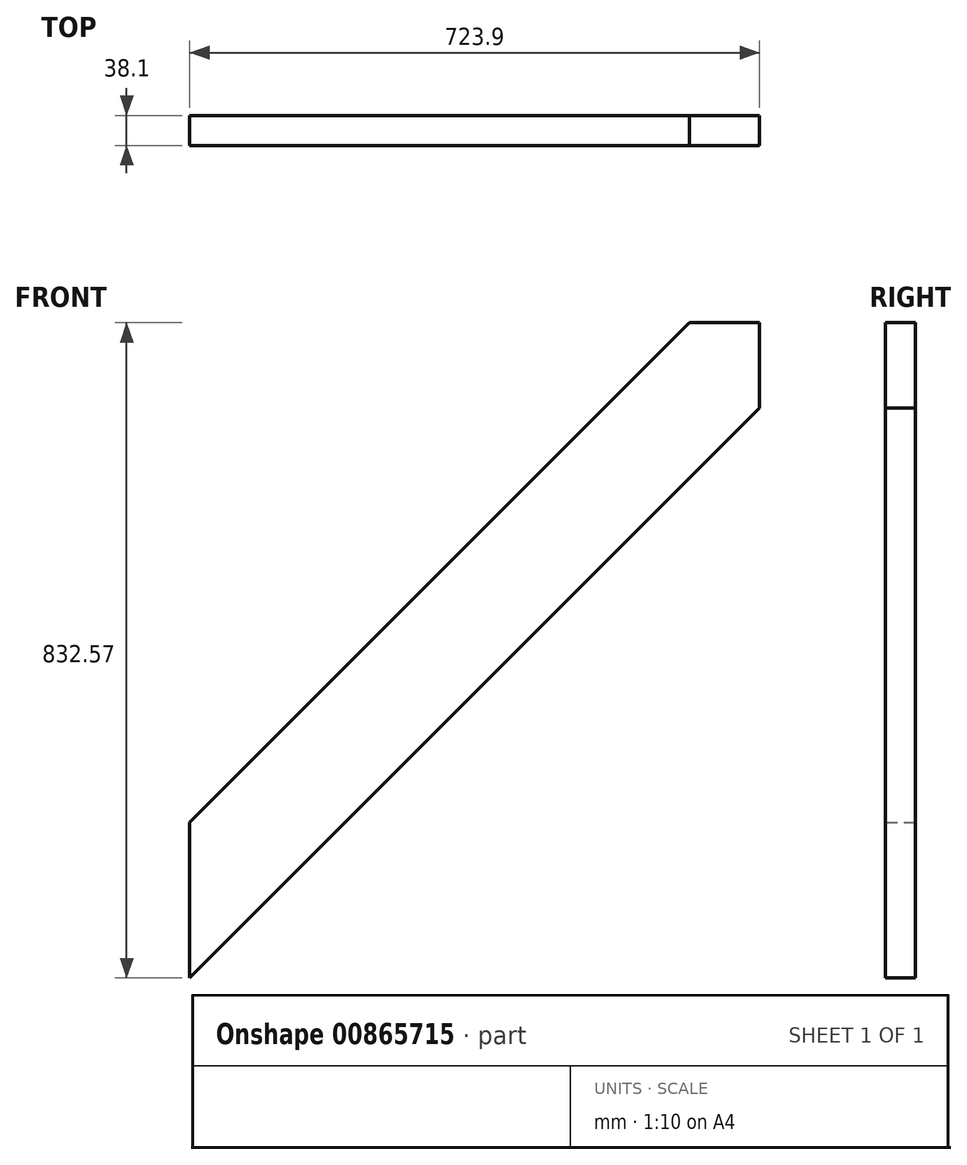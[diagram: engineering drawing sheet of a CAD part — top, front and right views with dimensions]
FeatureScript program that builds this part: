
annotation { "Feature Type Name" : "Feature", "Feature Type Description" : "" }
export const myFeature = defineFeature(function(context is Context, id is Id, definition is map)
    precondition{}
    {
        {
            var Q0;
            Q0=qCreatedBy(makeId("Front.planeOp"),FACE);
            var sketch = newSketch(context, id + "F0", { "sketchPlane" : qUnion([Q0])});
            skLineSegment(sketch, "E0", {"start": v(0, 0) * mm, "end": v(0, 197.57) * mm});
            skLineSegment(sketch, "E1", {"start": v(0, 197.57) * mm, "end": v(635, 832.57) * mm});
            skLineSegment(sketch, "E2", {"start": v(635, 832.57) * mm, "end": v(723.9, 832.57) * mm});
            skLineSegment(sketch, "E3", {"start": v(723.9, 832.57) * mm, "end": v(723.9, 723.9) * mm});
            skLineSegment(sketch, "E4", {"start": v(723.9, 723.9) * mm, "end": v(0, 0) * mm});
            skSolve(sketch);
        }
        {
            var Q0;
            Q0=makeQuery(id+"F0.imprint","IMPRINT",FACE,{"disambiguationData":[TD([[makeQuery(id+"F0.imprint","IMPRINT",EDGE,{"derivedFrom":sQuery(id+"F0.wireOp",EDGE,"E0")}),-1.0]])]});
            extrude(context, id + "F1", {"entities" : qUnion([Q0]), "depth" : 38.1 * mm, "offsetDistance" : 25.4 * mm});
        }
    });
